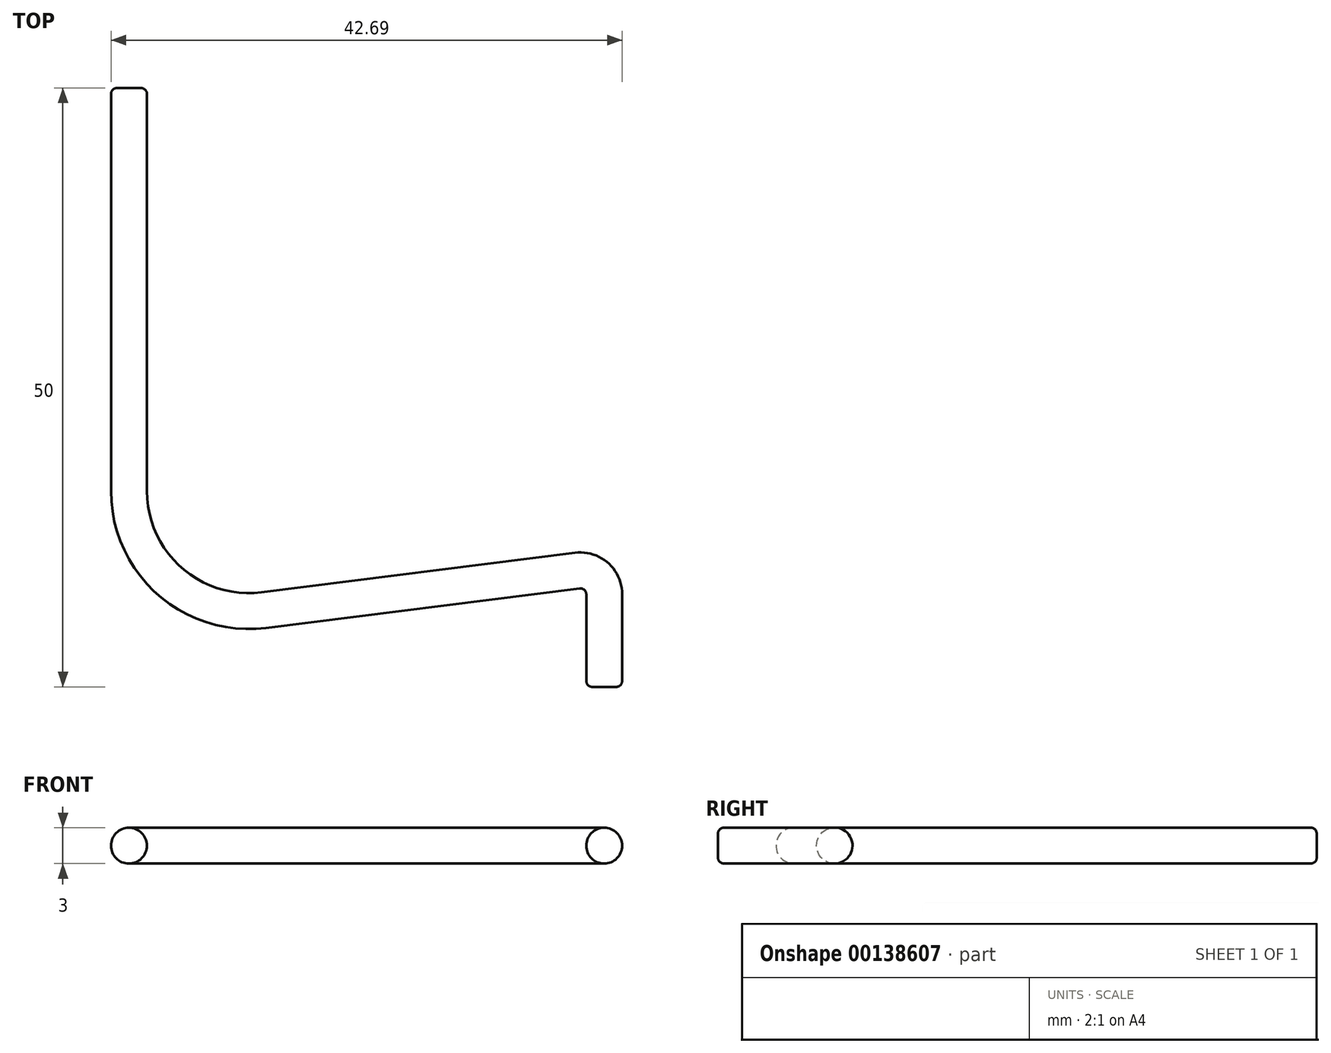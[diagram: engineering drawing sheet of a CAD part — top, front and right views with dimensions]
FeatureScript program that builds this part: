
annotation { "Feature Type Name" : "Feature", "Feature Type Description" : "" }
export const myFeature = defineFeature(function(context is Context, id is Id, definition is map)
    precondition{}
    {
        {
            assignVariable(context, id + "F0", {"name" : "pin_end_fillet", "anyValue" : 0.5 * mm});
        }
        {
            var Q0;
            Q0=qCreatedBy(makeId("Top.planeOp"),FACE);
            var sketch = newSketch(context, id + "F1", { "sketchPlane" : qUnion([Q0])});
            skLineSegment(sketch, "E0", {"start": v(-39.69, 50) * mm, "end": v(-39.69, 16.34) * mm});
            skLineSegment(sketch, "E1", {"start": v(-28.44, 6.42) * mm, "end": v(-2.25, 9.72) * mm});
            skLineSegment(sketch, "E2", {"start": v(0, 7.73) * mm, "end": v(0, 0) * mm});
            skPoint(sketch, "E3.visualSharp", {"position": v(-39.69, 5) * mm});
            skArc(sketch, "E3.filletArc", {"start": v(-39.69, 16.34) * mm, "mid": v(-36.3, 8.84) * mm, "end": v(-28.44, 6.42) * mm});
            skPoint(sketch, "E4.visualSharp", {"position": v(0, 10) * mm});
            skArc(sketch, "E5.filletArc", {"start": v(0, 7.73) * mm, "mid": v(-0.68, 9.23) * mm, "end": v(-2.25, 9.72) * mm});
            skSolve(sketch);
        }
        {
            var Q0;
            Q0=qCreatedBy(makeId("Front.planeOp"),FACE);
            cPlane(context, id + "F2", {"entities" : qUnion([Q0]), "cplaneType" : CPlaneType.OFFSET, "offset" : 50 * mm, "oppositeDirection" : true, "width" : 152.4 * mm, "height" : 152.4 * mm});
        }
        {
            var Q0;
            Q0=qCreatedBy(id+"F2.planeOp",FACE);
            var sketch = newSketch(context, id + "F3", { "sketchPlane" : qUnion([Q0])});
            skCircle(sketch, "E6", {"center": v(-39.69, 0) * mm, "radius": 1.5 * mm});
            skSolve(sketch);
        }
        {
            var Q0;
            Q0=makeQuery(id+"F3.imprint","IMPRINT",FACE,{"disambiguationData":[TD([[makeQuery(id+"F3.imprint","IMPRINT",EDGE,{"derivedFrom":sQuery(id+"F3.wireOp",EDGE,"E6")}),1.0]])]});
            var Q1;
            Q1=sQuery(id+"F1.wireOp",EDGE,"E0");
            var Q2;
            Q2=sQuery(id+"F1.wireOp",EDGE,"E3.filletArc");
            var Q3;
            Q3=sQuery(id+"F1.wireOp",EDGE,"E1");
            var Q4;
            Q4=sQuery(id+"F1.wireOp",EDGE,"E5.filletArc");
            var Q5;
            Q5=sQuery(id+"F1.wireOp",EDGE,"E2");
            sweep(context, id + "F4", {"profiles" : qUnion([Q0]), "path" : qUnion([Q1, Q2, Q3, Q4, Q5])});
        }
        {
            var Q0;
            Q0=makeQuery(id+"F4.opSweep","CAP_EDGE",EDGE,{"disambiguationData":[OSD([sQuery(id+"F1.wireOp",VERTEX,"E0.start"),sQuery(id+"F3.wireOp",EDGE,"E6")])],"isStart":true});
            var Q1;
            Q1=makeQuery(id+"F4.opSweep","CAP_EDGE",EDGE,{"disambiguationData":[OSD([sQuery(id+"F1.wireOp",VERTEX,"E2.end"),sQuery(id+"F3.wireOp",EDGE,"E6")])],"isStart":false});
            fillet(context, id + "F5", {"entities" : qUnion([Q0, Q1]), "radius" : getVariable(context, 'pin_end_fillet'), "tangentPropagation" : true, "allowEdgeOverflow" : false});
        }
    });
